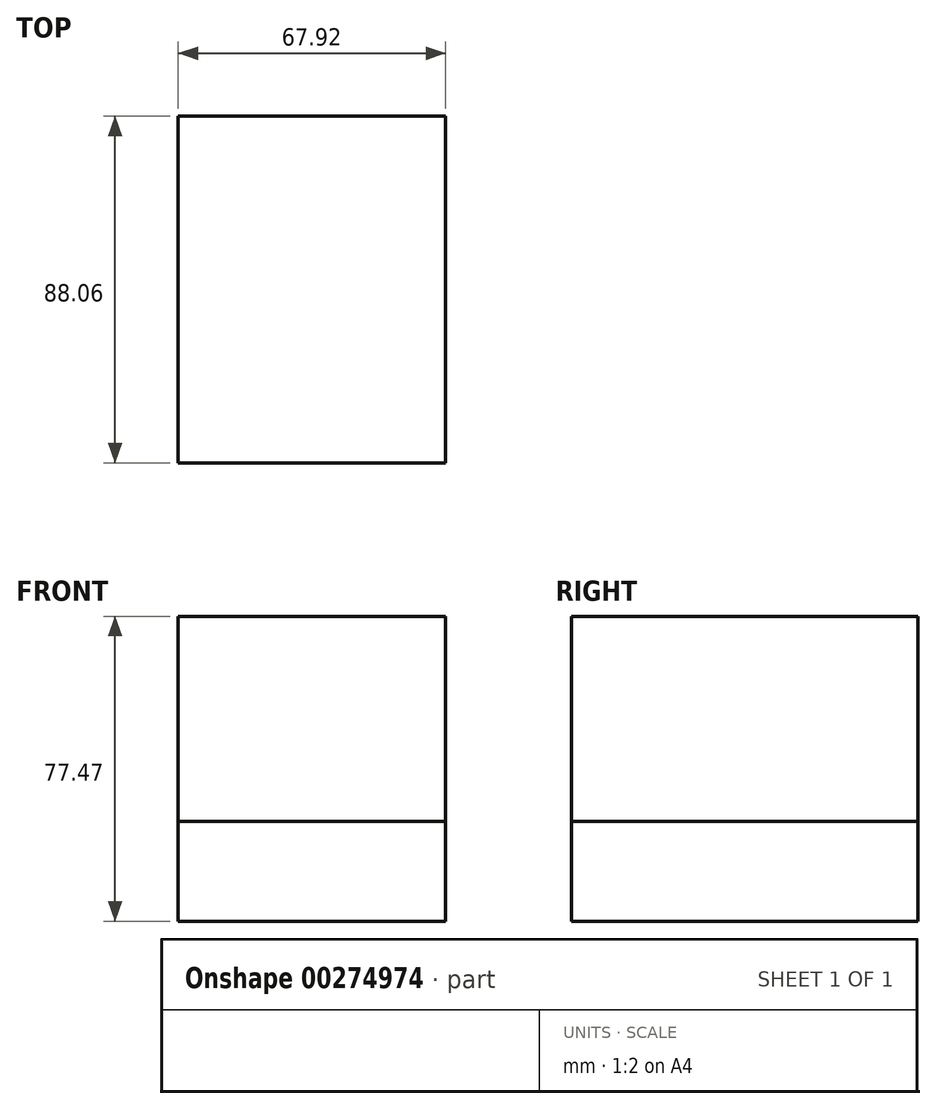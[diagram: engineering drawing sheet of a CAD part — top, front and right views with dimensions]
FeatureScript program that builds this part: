
annotation { "Feature Type Name" : "Feature", "Feature Type Description" : "" }
export const myFeature = defineFeature(function(context is Context, id is Id, definition is map)
    precondition{}
    {
        {
            var Q0;
            Q0=qCreatedBy(makeId("Top.planeOp"),FACE);
            var sketch = newSketch(context, id + "F0", { "sketchPlane" : qUnion([Q0])});
            skLineSegment(sketch, "E0.bottom", {"start": v(33.96, 44.03) * mm, "end": v(-33.96, 44.03) * mm});
            skLineSegment(sketch, "E0.top", {"start": v(33.96, -44.03) * mm, "end": v(-33.96, -44.03) * mm});
            skLineSegment(sketch, "E0.left", {"start": v(33.96, 44.03) * mm, "end": v(33.96, -44.03) * mm});
            skLineSegment(sketch, "E0.right", {"start": v(-33.96, 44.03) * mm, "end": v(-33.96, -44.03) * mm});
            skPoint(sketch, "E0.middle", {"position": v(0, 0) * mm});
            skSolve(sketch);
        }
        {
            var Q0;
            Q0 = qSketchRegion(id + "F0", true);
            extrude(context, id + "F1", {"entities" : qUnion([Q0]), "depth" : 45.2 * mm});
        }
        {
            var Q0;
            Q0=makeQuery(id+"F1.opExtrude","CAP_FACE",FACE,{"disambiguationData":[OSD([sQuery(id+"F0.wireOp",EDGE,"E0.bottom"),sQuery(id+"F0.wireOp",EDGE,"E0.top"),sQuery(id+"F0.wireOp",EDGE,"E0.left"),sQuery(id+"F0.wireOp",EDGE,"E0.right")])],"isStart":false});
            extrude(context, id + "F2", {"entities" : qUnion([Q0]), "operationType" : NewBodyOperationType.ADD, "depth" : 32.26 * mm});
        }
        {
            var Q0;
            Q0=makeQuery(id+"F0.imprint","IMPRINT",FACE,{"disambiguationData":[TD([[makeQuery(id+"F0.imprint","IMPRINT",EDGE,{"derivedFrom":sQuery(id+"F0.wireOp",EDGE,"E0.bottom")}),1.0]])]});
            extrude(context, id + "F3", {"entities" : qUnion([Q0]), "depth" : 25.4 * mm});
        }
    });
